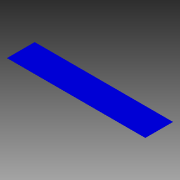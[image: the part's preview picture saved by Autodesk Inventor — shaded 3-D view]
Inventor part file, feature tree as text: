
AUTODESK INVENTOR PART (.ipt)
format: ipt  version: 2014 (Build 180170000, 170)  size: 79,872 bytes
history: native  units: mm
features: extrude x1, sketch x1
ambient origin geometry x8: Origin, YZ Plane, XZ Plane, XY Plane, X Axis, Y Axis, Z Axis, Center Point
bodies: Solid1 (feature_tree)
feature tree (2):
  extrude  "Extrusion1"  Depth=20000.0mm
  sketch  "Sketch2"  dims[d0=100000.0mm d1=20000.0mm d2=40.0mm d3=0.0mm]
